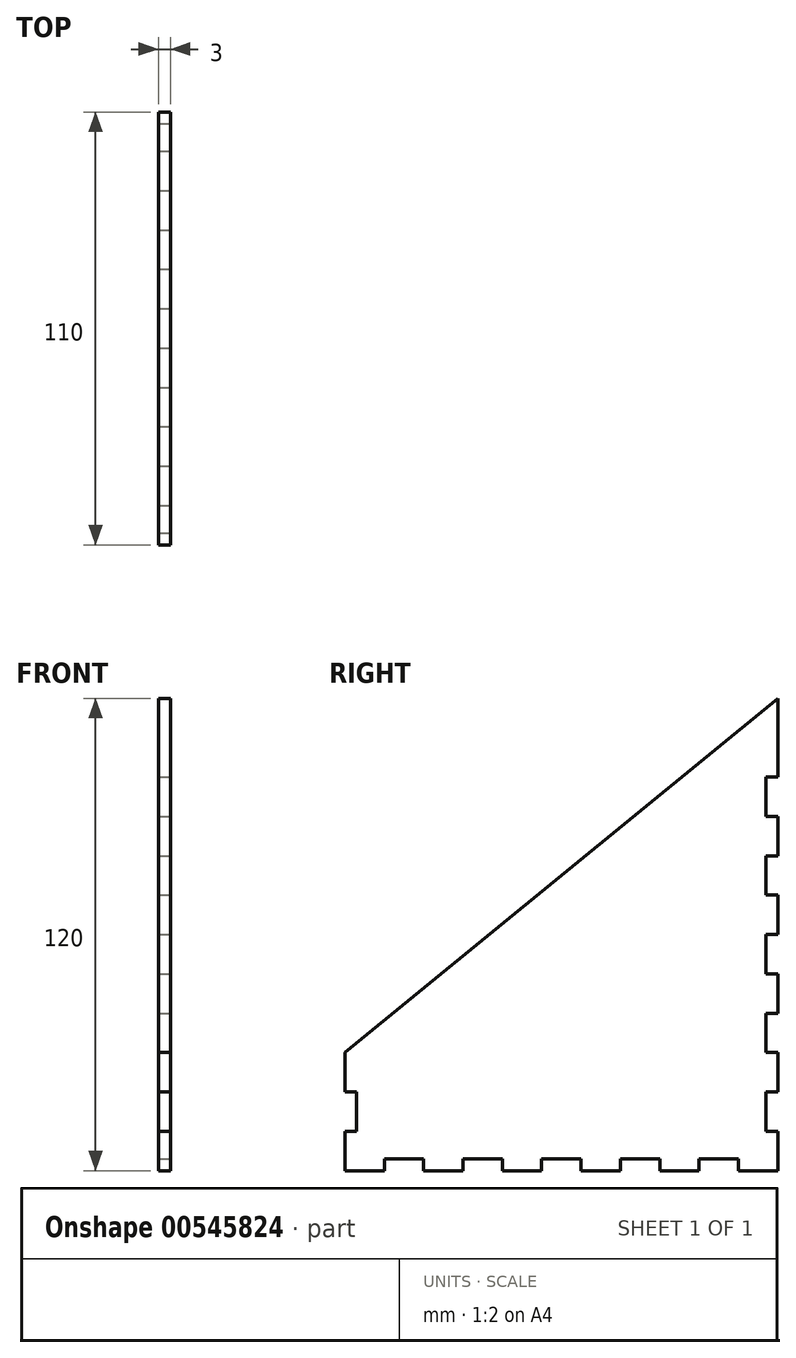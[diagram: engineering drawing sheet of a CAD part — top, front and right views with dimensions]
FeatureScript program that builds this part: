
annotation { "Feature Type Name" : "Feature", "Feature Type Description" : "" }
export const myFeature = defineFeature(function(context is Context, id is Id, definition is map)
    precondition{}
    {
        {
            var Q0;
            Q0=qCreatedBy(makeId("Right.planeOp"),FACE);
            var sketch = newSketch(context, id + "F0", { "sketchPlane" : qUnion([Q0])});
            skLineSegment(sketch, "E0", {"start": v(110, 0) * mm, "end": v(0, 0) * mm});
            skLineSegment(sketch, "E1", {"start": v(0, 0) * mm, "end": v(0, 30) * mm});
            skLineSegment(sketch, "E2", {"start": v(0, 30) * mm, "end": v(110, 120) * mm});
            skLineSegment(sketch, "E3", {"start": v(110, 120) * mm, "end": v(110, 0) * mm});
            skSolve(sketch);
        }
        {
            var Q0;
            Q0=makeQuery(id+"F0.imprint","IMPRINT",FACE,{"disambiguationData":[TD([[makeQuery(id+"F0.imprint","IMPRINT",EDGE,{"derivedFrom":sQuery(id+"F0.wireOp",EDGE,"E0")}),-1.0]])]});
            extrude(context, id + "F1", {"entities" : qUnion([Q0]), "depth" : 3 * mm, "offsetDistance" : 25 * mm});
        }
        {
            var Q0;
            Q0=makeQuery(id+"F1.opExtrude","CAP_FACE",FACE,{"disambiguationData":[OSD([sQuery(id+"F0.wireOp",EDGE,"E0"),sQuery(id+"F0.wireOp",EDGE,"E1"),sQuery(id+"F0.wireOp",EDGE,"E2"),sQuery(id+"F0.wireOp",EDGE,"E3")])],"isStart":false});
            var sketch = newSketch(context, id + "F2", { "sketchPlane" : qUnion([Q0])});
            skLineSegment(sketch, "E4.top", {"start": v(10, 3) * mm, "end": v(20, 3) * mm});
            skLineSegment(sketch, "E4.left", {"start": v(10, 0) * mm, "end": v(10, 3) * mm});
            skLineSegment(sketch, "E4.right", {"start": v(20, 0) * mm, "end": v(20, 3) * mm});
            skLineSegment(sketch, "E5", {"start": v(10, 0) * mm, "end": v(20, 0) * mm});
            skLineSegment(sketch, "E6.1.0.0", {"start": v(30, 0) * mm, "end": v(30, 3) * mm});
            skLineSegment(sketch, "E6.1.0.1", {"start": v(40, 0) * mm, "end": v(40, 3) * mm});
            skLineSegment(sketch, "E6.1.0.2", {"start": v(30, 3) * mm, "end": v(40, 3) * mm});
            skLineSegment(sketch, "E6.1.0.3", {"start": v(30, 0) * mm, "end": v(40, 0) * mm});
            skLineSegment(sketch, "E6.2.0.0", {"start": v(50, 0) * mm, "end": v(50, 3) * mm});
            skLineSegment(sketch, "E6.2.0.1", {"start": v(60, 0) * mm, "end": v(60, 3) * mm});
            skLineSegment(sketch, "E6.2.0.2", {"start": v(50, 3) * mm, "end": v(60, 3) * mm});
            skLineSegment(sketch, "E6.2.0.3", {"start": v(50, 0) * mm, "end": v(60, 0) * mm});
            skLineSegment(sketch, "E6.3.0.0", {"start": v(70, 0) * mm, "end": v(70, 3) * mm});
            skLineSegment(sketch, "E6.3.0.1", {"start": v(80, 0) * mm, "end": v(80, 3) * mm});
            skLineSegment(sketch, "E6.3.0.2", {"start": v(70, 3) * mm, "end": v(80, 3) * mm});
            skLineSegment(sketch, "E6.3.0.3", {"start": v(70, 0) * mm, "end": v(80, 0) * mm});
            skLineSegment(sketch, "E6.4.0.0", {"start": v(90, 0) * mm, "end": v(90, 3) * mm});
            skLineSegment(sketch, "E6.4.0.1", {"start": v(100, 0) * mm, "end": v(100, 3) * mm});
            skLineSegment(sketch, "E6.4.0.2", {"start": v(90, 3) * mm, "end": v(100, 3) * mm});
            skLineSegment(sketch, "E6.4.0.3", {"start": v(90, 0) * mm, "end": v(100, 0) * mm});
            skLineSegment(sketch, "E6.direction1", {"start": v(10, 0) * mm, "end": v(30, 0) * mm, "construction": true});
            skSolve(sketch);
        }
        {
            var Q0;
            Q0 = qSketchRegion(id + "F2", true);
            extrude(context, id + "F3", {"entities" : qUnion([Q0]), "operationType" : NewBodyOperationType.REMOVE, "oppositeDirection" : true, "depth" : 25 * mm, "offsetDistance" : 25 * mm});
        }
        {
            var Q0;
            Q0=makeQuery(id+"F1.opExtrude","CAP_FACE",FACE,{"disambiguationData":[OSD([sQuery(id+"F0.wireOp",EDGE,"E0"),sQuery(id+"F0.wireOp",EDGE,"E1"),sQuery(id+"F0.wireOp",EDGE,"E2"),sQuery(id+"F0.wireOp",EDGE,"E3")])],"isStart":false});
            var sketch = newSketch(context, id + "F4", { "sketchPlane" : qUnion([Q0])});
            skLineSegment(sketch, "E7.bottom", {"start": v(0, 10) * mm, "end": v(3, 10) * mm});
            skLineSegment(sketch, "E7.top", {"start": v(0, 20) * mm, "end": v(3, 20) * mm});
            skLineSegment(sketch, "E7.left", {"start": v(0, 10) * mm, "end": v(0, 20) * mm});
            skLineSegment(sketch, "E7.right", {"start": v(3, 10) * mm, "end": v(3, 20) * mm});
            skSolve(sketch);
        }
        {
            var Q0;
            Q0 = qSketchRegion(id + "F4", true);
            extrude(context, id + "F5", {"entities" : qUnion([Q0]), "operationType" : NewBodyOperationType.REMOVE, "oppositeDirection" : true, "depth" : 25 * mm, "offsetDistance" : 25 * mm});
        }
        {
            var Q0;
            Q0=makeQuery(id+"F1.opExtrude","CAP_FACE",FACE,{"disambiguationData":[OSD([sQuery(id+"F0.wireOp",EDGE,"E0"),sQuery(id+"F0.wireOp",EDGE,"E1"),sQuery(id+"F0.wireOp",EDGE,"E2"),sQuery(id+"F0.wireOp",EDGE,"E3")])],"isStart":false});
            var sketch = newSketch(context, id + "F6", { "sketchPlane" : qUnion([Q0])});
            skLineSegment(sketch, "E8.bottom", {"start": v(110, 10) * mm, "end": v(107, 10) * mm});
            skLineSegment(sketch, "E8.top", {"start": v(110, 20) * mm, "end": v(107, 20) * mm});
            skLineSegment(sketch, "E8.left", {"start": v(110, 10) * mm, "end": v(110, 20) * mm});
            skLineSegment(sketch, "E8.right", {"start": v(107, 10) * mm, "end": v(107, 20) * mm});
            skLineSegment(sketch, "E9.0.1.0", {"start": v(107, 30) * mm, "end": v(107, 40) * mm});
            skLineSegment(sketch, "E9.0.1.1", {"start": v(110, 30) * mm, "end": v(110, 40) * mm});
            skLineSegment(sketch, "E9.0.1.2", {"start": v(110, 40) * mm, "end": v(107, 40) * mm});
            skLineSegment(sketch, "E9.0.1.3", {"start": v(110, 30) * mm, "end": v(107, 30) * mm});
            skLineSegment(sketch, "E9.0.2.0", {"start": v(107, 50) * mm, "end": v(107, 60) * mm});
            skLineSegment(sketch, "E9.0.2.1", {"start": v(110, 50) * mm, "end": v(110, 60) * mm});
            skLineSegment(sketch, "E9.0.2.2", {"start": v(110, 60) * mm, "end": v(107, 60) * mm});
            skLineSegment(sketch, "E9.0.2.3", {"start": v(110, 50) * mm, "end": v(107, 50) * mm});
            skLineSegment(sketch, "E9.0.3.0", {"start": v(107, 70) * mm, "end": v(107, 80) * mm});
            skLineSegment(sketch, "E9.0.3.1", {"start": v(110, 70) * mm, "end": v(110, 80) * mm});
            skLineSegment(sketch, "E9.0.3.2", {"start": v(110, 80) * mm, "end": v(107, 80) * mm});
            skLineSegment(sketch, "E9.0.3.3", {"start": v(110, 70) * mm, "end": v(107, 70) * mm});
            skLineSegment(sketch, "E9.0.4.0", {"start": v(107, 90) * mm, "end": v(107, 100) * mm});
            skLineSegment(sketch, "E9.0.4.1", {"start": v(110, 90) * mm, "end": v(110, 100) * mm});
            skLineSegment(sketch, "E9.0.4.2", {"start": v(110, 100) * mm, "end": v(107, 100) * mm});
            skLineSegment(sketch, "E9.0.4.3", {"start": v(110, 90) * mm, "end": v(107, 90) * mm});
            skLineSegment(sketch, "E9.direction1", {"start": v(107, 10) * mm, "end": v(132, 10) * mm, "construction": true});
            skLineSegment(sketch, "E9.direction2", {"start": v(107, 10) * mm, "end": v(107, 30) * mm, "construction": true});
            skSolve(sketch);
        }
        {
            var Q0;
            Q0=makeQuery(id+"F6.imprint","IMPRINT",FACE,{"disambiguationData":[TD([[makeQuery(id+"F6.imprint","IMPRINT",EDGE,{"derivedFrom":sQuery(id+"F6.wireOp",EDGE,"E8.bottom")}),-1.0]])]});
            var Q1;
            Q1=makeQuery(id+"F6.imprint","IMPRINT",FACE,{"disambiguationData":[TD([[makeQuery(id+"F6.imprint","IMPRINT",EDGE,{"derivedFrom":sQuery(id+"F6.wireOp",EDGE,"E9.0.1.0")}),-1.0]])]});
            var Q2;
            Q2=makeQuery(id+"F6.imprint","IMPRINT",FACE,{"disambiguationData":[TD([[makeQuery(id+"F6.imprint","IMPRINT",EDGE,{"derivedFrom":sQuery(id+"F6.wireOp",EDGE,"E9.0.2.0")}),-1.0]])]});
            var Q3;
            Q3=makeQuery(id+"F6.imprint","IMPRINT",FACE,{"disambiguationData":[TD([[makeQuery(id+"F6.imprint","IMPRINT",EDGE,{"derivedFrom":sQuery(id+"F6.wireOp",EDGE,"E9.0.3.0")}),-1.0]])]});
            var Q4;
            Q4=makeQuery(id+"F6.imprint","IMPRINT",FACE,{"disambiguationData":[TD([[makeQuery(id+"F6.imprint","IMPRINT",EDGE,{"derivedFrom":sQuery(id+"F6.wireOp",EDGE,"E9.0.4.0")}),-1.0]])]});
            extrude(context, id + "F7", {"entities" : qUnion([Q0, Q1, Q2, Q3, Q4]), "operationType" : NewBodyOperationType.REMOVE, "oppositeDirection" : true, "depth" : 25 * mm, "offsetDistance" : 25 * mm});
        }
    });
